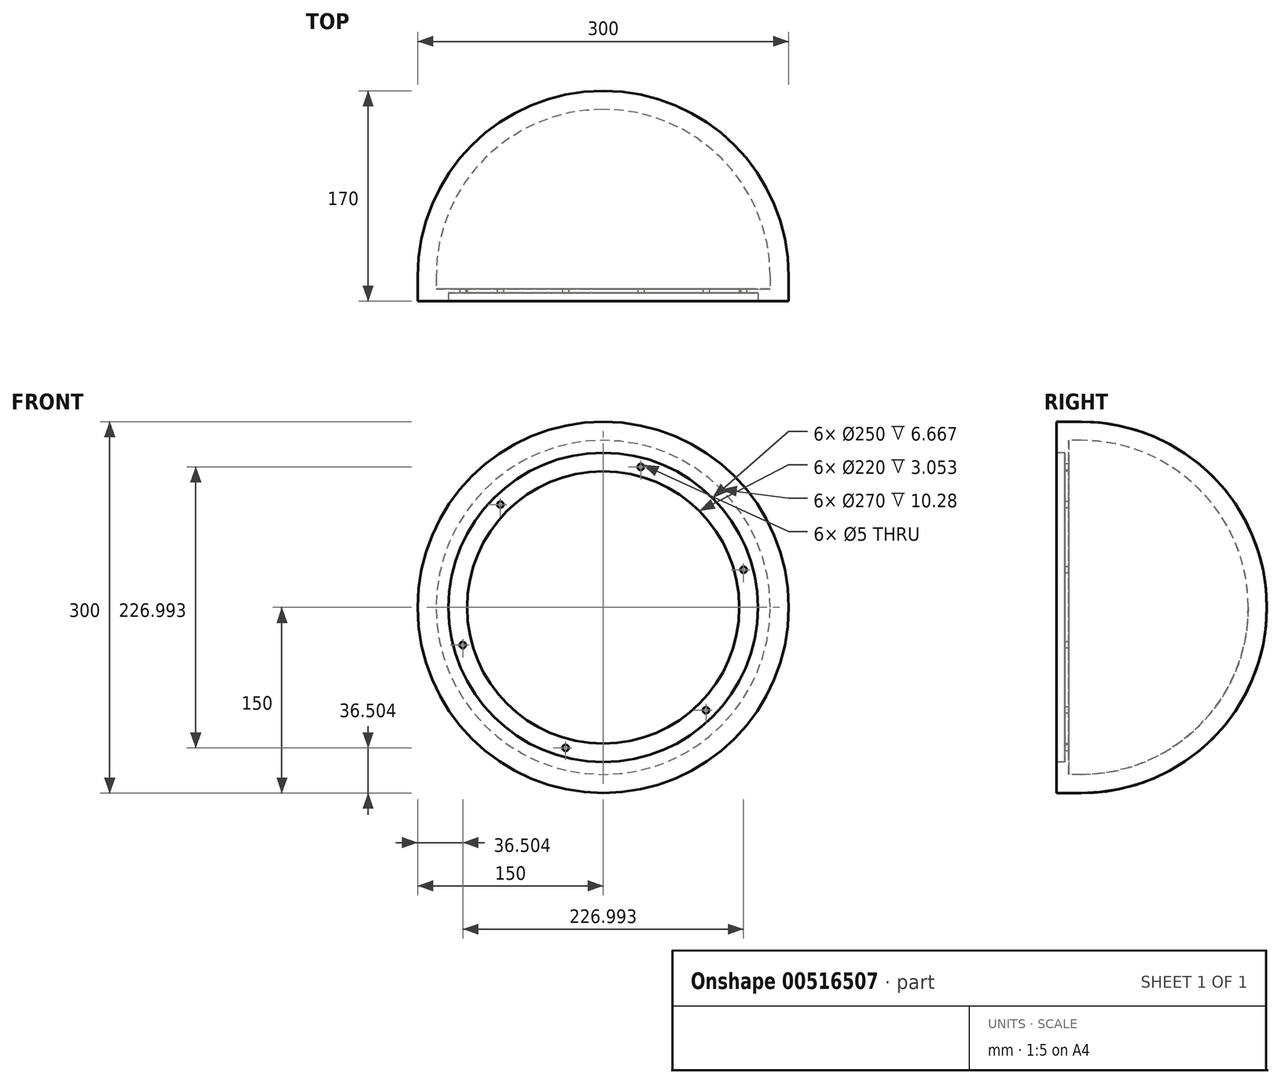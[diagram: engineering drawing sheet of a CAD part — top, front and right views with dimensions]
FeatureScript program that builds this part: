
annotation { "Feature Type Name" : "Feature", "Feature Type Description" : "" }
export const myFeature = defineFeature(function(context is Context, id is Id, definition is map)
    precondition{}
    {
        {
            var Q0;
            Q0=qCreatedBy(makeId("Front.planeOp"),FACE);
            var sketch = newSketch(context, id + "F0", { "sketchPlane" : qUnion([Q0])});
            skCircle(sketch, "E0", {"center": v(0, 0) * mm, "radius": 150 * mm});
            skCircle(sketch, "E1", {"center": v(0, 0) * mm, "radius": 125 * mm});
            skCircle(sketch, "E2", {"center": v(0, 0) * mm, "radius": 110 * mm});
            skPoint(sketch, "E3.2.0", {"position": v(-83.09, 83.09) * mm});
            skSolve(sketch);
        }
        {
            var Q0;
            Q0=qCreatedBy(makeId("Right.planeOp"),FACE);
            var sketch = newSketch(context, id + "F1", { "sketchPlane" : qUnion([Q0])});
            skLineSegment(sketch, "E4", {"start": v(0, 0) * mm, "end": v(0, 150) * mm});
            skLineSegment(sketch, "E5", {"start": v(0, 150) * mm, "end": v(20, 150) * mm});
            skLineSegment(sketch, "E6", {"start": v(0, 125) * mm, "end": v(6.67, 125) * mm});
            skLineSegment(sketch, "E7", {"start": v(6.67, 125) * mm, "end": v(6.67, 110) * mm});
            skLineSegment(sketch, "E8", {"start": v(6.67, 110) * mm, "end": v(9.72, 110) * mm});
            skLineSegment(sketch, "E9", {"start": v(20, 135) * mm, "end": v(20, 150) * mm});
            skLineSegment(sketch, "E10", {"start": v(-69.67, 0) * mm, "end": v(182.78, 0) * mm, "construction": true});
            skPoint(sketch, "E11", {"position": v(20, 0) * mm});
            skArc(sketch, "E12", {"start": v(20, 150) * mm, "mid": v(126.07, 106.07) * mm, "end": v(170, 0) * mm});
            skArc(sketch, "E13", {"start": v(20, 135) * mm, "mid": v(115.46, 95.46) * mm, "end": v(155, 0) * mm});
            skLineSegment(sketch, "E14", {"start": v(155, 0) * mm, "end": v(170, 0) * mm, "construction": true});
            skLineSegment(sketch, "E15", {"start": v(170, 0) * mm, "end": v(155, 0) * mm});
            skLineSegment(sketch, "E16", {"start": v(9.72, 110) * mm, "end": v(9.72, 135) * mm});
            skLineSegment(sketch, "E17", {"start": v(9.72, 135) * mm, "end": v(20, 135) * mm});
            skSolve(sketch);
        }
        {
            var Q0;
            Q0=makeQuery(id+"F1.imprint","IMPRINT",FACE,{"disambiguationData":[TD([[makeQuery(id+"F1.imprint","IMPRINT",EDGE,{"derivedFrom":sQuery(id+"F1.wireOp",EDGE,"E9")}),-1.0]])]});
            var Q1;
            {var subQ1=sQuery(id+"F1.wireOp",EDGE,"E5");Q1=makeQuery(id+"F1.imprint","IMPRINT",FACE,{"disambiguationData":[TD([[makeQuery(id+"F1.imprint","IMPRINT",EDGE,{"derivedFrom":subQ1}),-1.0]])]});}
            var Q2;
            Q2=sQuery(id+"F1.wireOp",EDGE,"E10");
            revolve(context, id + "F2", {"entities" : qUnion([Q0, Q1]), "axis" : qUnion([Q2]), "revolveType" : RevolveType.FULL});
        }
        {
            var Q0;
            Q0=sQuery(id+"F0.wireOp",VERTEX,"E3.2.0");
            var Q1;
            Q1=makeQuery(id+"F2.opRevolve","SWEPT_BODY",BODY,{"disambiguationData":[OSD([sQuery(id+"F1.wireOp",EDGE,"E4"),sQuery(id+"F1.wireOp",EDGE,"E5"),sQuery(id+"F1.wireOp",EDGE,"E6"),sQuery(id+"F1.wireOp",EDGE,"E7"),sQuery(id+"F1.wireOp",EDGE,"E8"),sQuery(id+"F1.wireOp",EDGE,"E12"),sQuery(id+"F1.wireOp",EDGE,"E13"),sQuery(id+"F1.wireOp",EDGE,"E15"),sQuery(id+"F1.wireOp",EDGE,"E16"),sQuery(id+"F1.wireOp",EDGE,"E17")])]});
            hole(context, id + "F3", {"style" : HoleStyle.SIMPLE, "endStyle" : HoleEndStyle.BLIND, "holeDiameter" : 5 * mm, "holeDepth" : 12 * mm, "isTappedThrough" : true, "tappedDepth" : 12 * mm, "tapClearance" : 3, "locations" : qUnion([Q0]), "scope" : qUnion([Q1])});
        }
        {
            var Q0;
            Q0=makeQuery(id+"F2.opRevolve","SWEPT_BODY",BODY,{"disambiguationData":[OSD([sQuery(id+"F1.wireOp",EDGE,"E4"),sQuery(id+"F1.wireOp",EDGE,"E5"),sQuery(id+"F1.wireOp",EDGE,"E6"),sQuery(id+"F1.wireOp",EDGE,"E7"),sQuery(id+"F1.wireOp",EDGE,"E8"),sQuery(id+"F1.wireOp",EDGE,"E12"),sQuery(id+"F1.wireOp",EDGE,"E13"),sQuery(id+"F1.wireOp",EDGE,"E15"),sQuery(id+"F1.wireOp",EDGE,"E16"),sQuery(id+"F1.wireOp",EDGE,"E17")])]});
            var Q1;
            Q1=sQuery(id+"F1.wireOp",EDGE,"E10");
            circularPattern(context, id + "F4", {"entities" : qUnion([Q0]), "axis" : qUnion([Q1]), "angle" : 360 * degree, "instanceCount" : 6, "equalSpace" : true});
        }
    });
